# Revit family: ОНФ
name_source: partatom
category: Оборудование
units: mm (PartAtom-declared; Revit-internal decimal feet)

## family parameters
Всегда вертикально = Да
Классификация = Нет
На основе рабочей плоскости = Нет
Общий = Нет
При загрузке вырезать с полостями = Нет
Размер круглого соединителя = Использовать диаметр
Тип детали = Нормальный
Точка принадлежности помещению = Нет

## types (15) — shared parameters
00_20_Manufacturer = Вентс
00_20_Name = Припливно-витяжна решітка
Casing Material = Металл, окрашенный, синий, матовый RAL 5007
Grid Material = Cover Grid Cross
Load Classification = HVAC
Maintenance zone material = <По категории>
Maximum Air Flow = 0.0 м³/ч
S = 6 мм
r = 5 мм
Вага = 6.50 кг
zero-valued in all types: Отметка по умолчанию

## per-type parameters (varying)
| type | A | A1 | A2 | B | B1 | B2 | C | a1 | a2 | n | t |
| ОНФ 100х100 | 100 мм | 80 мм | 90 мм | 100 мм | 80 мм | 90 мм | 10 мм | 40 мм | -40 мм | 13 | 2 мм |
| ОНФ 1000х1000 | 1000 мм | 940 мм | 970 мм | 1000 мм | 940 мм | 970 мм | 30 мм | 470 мм | -470 мм | 157 | 3 мм |
| ОНФ 900х900 | 900 мм | 840 мм | 870 мм | 900 мм | 840 мм | 870 мм | 30 мм | 420 мм | -420 мм | 140 | 3 мм |
| ОНФ 800х800 | 800 мм | 740 мм | 770 мм | 800 мм | 740 мм | 770 мм | 30 мм | 370 мм | -370 мм | 123 | 3 мм |
| ОНФ 700х700 | 700 мм | 640 мм | 670 мм | 700 мм | 640 мм | 670 мм | 30 мм | 320 мм | -320 мм | 107 | 3 мм |
| ОНФ 600х600 | 600 мм | 540 мм | 570 мм | 600 мм | 540 мм | 570 мм | 30 мм | 270 мм | -270 мм | 90 | 3 мм |
| ОНФ 500х500 | 500 мм | 440 мм | 470 мм | 500 мм | 440 мм | 470 мм | 30 мм | 220 мм | -220 мм | 73 | 3 мм |
| ОНФ 400х400 | 300 мм | 250 мм | 275 мм | 300 мм | 250 мм | 275 мм | 25 мм | 125 мм | -125 мм | 42 | 3 мм |
| ОНФ 300х300 | 300 мм | 250 мм | 275 мм | 300 мм | 250 мм | 275 мм | 25 мм | 125 мм | -125 мм | 42 | 3 мм |
| ОНФ 200х200 | 200 мм | 160 мм | 180 мм | 200 мм | 160 мм | 180 мм | 20 мм | 80 мм | -80 мм | 27 | 3 мм |
| ОНФ 100х150 | 100 мм | 80 мм | 90 мм | 150 мм | 130 мм | 140 мм | 10 мм | 40 мм | -40 мм | 22 | 2 мм |
| ОНФ 150х150 | 150 мм | 130 мм | 140 мм | 150 мм | 130 мм | 140 мм | 10 мм | 65 мм | -65 мм | 22 | 2 мм |
| ОНФ 150х200 | 250 мм | 220 мм | 235 мм | 200 мм | 170 мм | 185 мм | 15 мм | 110 мм | -110 мм | 28 | 2 мм |
| ОНФ 900х400 | 900 мм | 840 мм | 870 мм | 400 мм | 340 мм | 370 мм | 30 мм | 420 мм | -420 мм | 57 | 3 мм |
| ОНФ 1000х400 | 1000 мм | 940 мм | 970 мм | 400 мм | 340 мм | 370 мм | 30 мм | 470 мм | -470 мм | 57 | 3 мм |

note: column(s) folded — value = type name in every type: 00_20_Type
